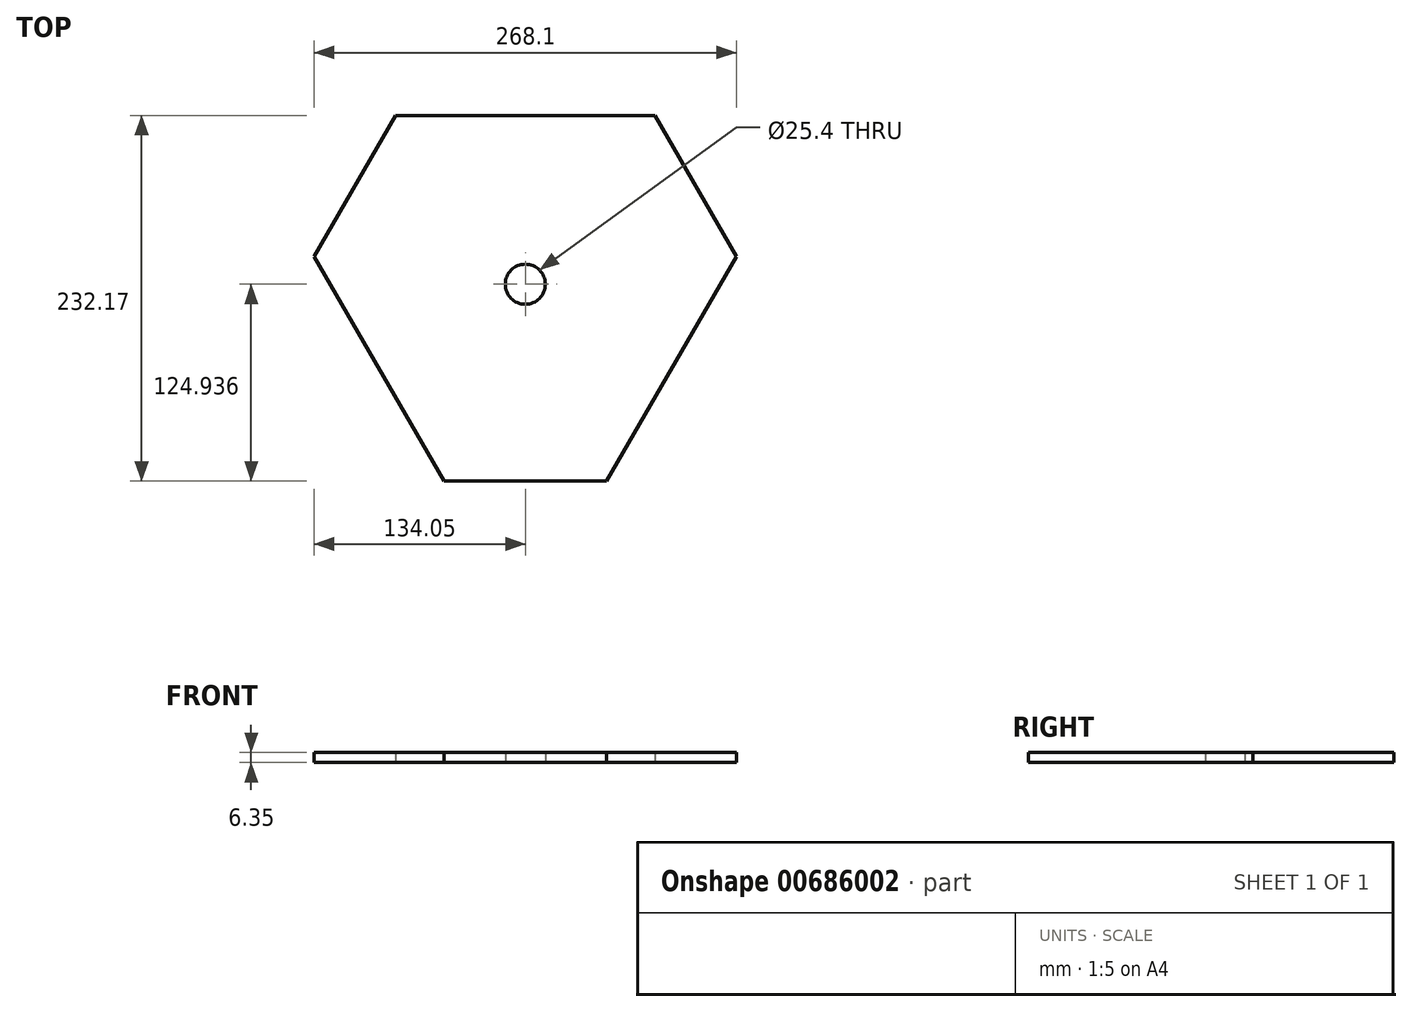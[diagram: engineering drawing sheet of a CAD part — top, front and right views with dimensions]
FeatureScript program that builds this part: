
annotation { "Feature Type Name" : "Feature", "Feature Type Description" : "" }
export const myFeature = defineFeature(function(context is Context, id is Id, definition is map)
    precondition{}
    {
        {
            var Q0;
            Q0=qCreatedBy(makeId("Top.planeOp"),FACE);
            var sketch = newSketch(context, id + "F0", { "sketchPlane" : qUnion([Q0])});
            skLineSegment(sketch, "E0", {"start": v(0, 140.37) * mm, "end": v(-177.8, -167.58) * mm});
            skLineSegment(sketch, "E1", {"start": v(-165.1, -189.58) * mm, "end": v(190.5, -189.58) * mm});
            skLineSegment(sketch, "E2", {"start": v(203.2, -167.58) * mm, "end": v(25.4, 140.37) * mm});
            skLineSegment(sketch, "E3", {"start": v(0, 140.37) * mm, "end": v(25.4, 140.37) * mm});
            skLineSegment(sketch, "E4", {"start": v(-177.8, -167.58) * mm, "end": v(-165.1, -189.58) * mm});
            skLineSegment(sketch, "E5", {"start": v(190.5, -189.58) * mm, "end": v(203.2, -167.58) * mm});
            skLineSegment(sketch, "E6", {"start": v(188.54, -142.18) * mm, "end": v(161.17, -189.58) * mm, "construction": true});
            skLineSegment(sketch, "E7", {"start": v(-163.14, -142.18) * mm, "end": v(-135.77, -189.58) * mm, "construction": true});
            skLineSegment(sketch, "E8", {"start": v(-14.66, 114.97) * mm, "end": v(40.06, 114.97) * mm, "construction": true});
            skLineSegment(sketch, "E9", {"start": v(142.35, -62.18) * mm, "end": v(68.8, -189.58) * mm});
            skLineSegment(sketch, "E10", {"start": v(-116.95, -62.18) * mm, "end": v(-43.4, -189.58) * mm});
            skLineSegment(sketch, "E11", {"start": v(-60.85, 34.97) * mm, "end": v(86.25, 34.97) * mm});
            skCircle(sketch, "E12", {"center": v(12.7, -72.26) * mm, "radius": 12.7 * mm});
            skLineSegment(sketch, "E13", {"start": v(12.7, -72.26) * mm, "end": v(-80.17, -125.88) * mm, "construction": true});
            skLineSegment(sketch, "E14", {"start": v(12.7, -72.26) * mm, "end": v(105.57, -125.88) * mm, "construction": true});
            skLineSegment(sketch, "E15", {"start": v(12.7, -72.26) * mm, "end": v(12.7, 34.97) * mm, "construction": true});
            skLineSegment(sketch, "E16", {"start": v(68.8, -189.58) * mm, "end": v(190.5, -189.58) * mm, "construction": true});
            skLineSegment(sketch, "E17", {"start": v(12.7, 177.61) * mm, "end": v(229.1, -197.2) * mm, "construction": true});
            skLineSegment(sketch, "E18", {"start": v(229.1, -197.2) * mm, "end": v(-203.7, -197.2) * mm, "construction": true});
            skLineSegment(sketch, "E19", {"start": v(-203.7, -197.2) * mm, "end": v(12.7, 177.61) * mm, "construction": true});
            skLineSegment(sketch, "E20", {"start": v(-43.4, -189.58) * mm, "end": v(-39, -197.2) * mm});
            skLineSegment(sketch, "E21", {"start": v(68.8, -189.58) * mm, "end": v(64.4, -197.2) * mm});
            skLineSegment(sketch, "E22", {"start": v(142.35, -62.18) * mm, "end": v(146.75, -54.56) * mm});
            skLineSegment(sketch, "E23", {"start": v(-116.95, -62.18) * mm, "end": v(-121.35, -54.56) * mm});
            skLineSegment(sketch, "E24", {"start": v(95.05, 34.97) * mm, "end": v(146.75, -54.56) * mm});
            skLineSegment(sketch, "E25", {"start": v(-39, -197.2) * mm, "end": v(64.4, -197.2) * mm});
            skLineSegment(sketch, "E26", {"start": v(-121.35, -54.56) * mm, "end": v(-69.65, 34.97) * mm});
            skLineSegment(sketch, "E27", {"start": v(-69.65, 34.97) * mm, "end": v(-60.85, 34.97) * mm});
            skLineSegment(sketch, "E28", {"start": v(86.25, 34.97) * mm, "end": v(95.05, 34.97) * mm});
            skSolve(sketch);
        }
        {
            var Q0;
            {var subQ0=sQuery(id+"F0.wireOp",EDGE,"E9");Q0=makeQuery(id+"F0.imprint","IMPRINT",FACE,{"disambiguationData":[TD([[makeQuery(id+"F0.imprint","IMPRINT",EDGE,{"derivedFrom":subQ0}),-1.0]])]});}
            var Q1;
            {var subQ0=sQuery(id+"F0.wireOp",EDGE,"E23");Q1=makeQuery(id+"F0.imprint","IMPRINT",FACE,{"disambiguationData":[TD([[makeQuery(id+"F0.imprint","IMPRINT",EDGE,{"derivedFrom":subQ0}),-1.0]])]});}
            var Q2;
            {var subQ0=sQuery(id+"F0.wireOp",EDGE,"E22");Q2=makeQuery(id+"F0.imprint","IMPRINT",FACE,{"disambiguationData":[TD([[makeQuery(id+"F0.imprint","IMPRINT",EDGE,{"derivedFrom":subQ0}),1.0]])]});}
            var Q3;
            {var subQ2=sQuery(id+"F0.wireOp",EDGE,"E20");Q3=makeQuery(id+"F0.imprint","IMPRINT",FACE,{"disambiguationData":[TD([[makeQuery(id+"F0.imprint","IMPRINT",EDGE,{"derivedFrom":subQ2}),1.0]])]});}
            extrude(context, id + "F1", {"entities" : qUnion([Q0, Q1, Q2, Q3]), "depth" : 6.35 * mm, "offsetDistance" : 25 * mm});
        }
    });
